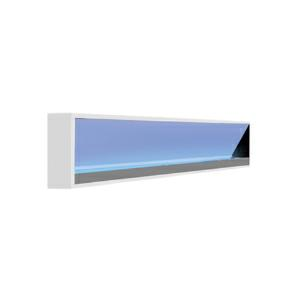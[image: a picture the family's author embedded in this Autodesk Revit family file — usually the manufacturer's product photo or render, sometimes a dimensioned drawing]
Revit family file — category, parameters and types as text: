
# Revit family: 3f_filippi_-_3f_violetta_uv-c_parete_3f_filippi_-_9302_-_3f_violetta_uvc_wall_1x30_t8_s-l_l925
name_source: partatom
category: Lighting Fixtures
units: mm (PartAtom-declared; Revit-internal decimal feet)

## family parameters
Cut with Voids When Loaded = No
Host = Face
Light Source = No
Part Type = Normal
Room Calculation Point = No
Round Connector Dimension = Use Diameter
Shared = No

## types (1)
- 3F Filippi - 3F Violetta UV-C Parete
    Apparent Load = 0 VA
    Approval mark = ENEC
    Default Elevation = 1800 mm
    Description = Room sterilization device, designed for the use of a T8 germicidal lamp.

ILLUMINOTECHNICAL
Luminous efficiency 62%.
Indirect asymmetric distribution for air sanitization.

SOURCE
Fixtures supplied without germicidal lamps (W/L); below are some lamps available from the main distributors of electrical material.
<ul><li>Osram PURITEC T8 - HNS 30W G13</li>
<li>Philips TUV T8 - TUV 30W 1SL/25 G13</li></ul>
Germicidal lamps are special lamps that produce ultraviolet radiation with domain spectral components in the UV-C range; this radiation modifies the DNA or RNA of microorganisms (bacteria, viruses, germ and mould spores) and prevents them from reproducing or being harmful.
Germicidal lamps emit high intensity UV-C radiation that can cause burns, eye irritation (conjunctivitis) and skin damage (erythema).

MECHANICAL
Body made of steel painted white with antimicrobial powder paint.
The particular paint, in addition to the antimicrobial properties, offers protection and decoration typical of a high-performance powder paint and is specific for use in areas where it is necessary to guarantee a high level of cleanliness, for example in the medical, food, public recreational sports areas and for crowded places such as public transport, airports, schools, etc.
The development and spread of microbes such as bacteria, and mould can affect the operation of a product, be responsible for degradation, bad smells and stains.
Cleaning actions are used to eliminate the presence of bacteria on products.
However, between one cleaning cycle and another microbes multiply on surfaces.
The antimicrobial protection acts between cleaning cycles to provide products with further defence against the development of bacteria.
Recuperator in satin anodised aluminium to avoid annoying reflections.
Internal black end caps.
Dimensions: 925x70 mm, height 180 mm. Weight 2.82 kg.
IP20 protection degree.
Glow-wire test resistance 960°C.

ELECTRICAL
EEI A2 Electronic wiring 230V-50/60Hz, class I.
Lamp warm start.
Double insulation silicone cabling with high resistance to UV.
Power of the luminaire 34 W.
CE - IEC 60598-1 - EN 60598-1.
Ambient temperature from 0°C to +25°C.

INSTALLATION
Wall.
Indirect asymmetric distribution for air sanitisation.
Mandatory orientation of the fixture with the lamp at the bottom; installation height of no less than 2 metres from the ground.

APPLICATIONS
Room disinfection fixtures designed to be used with germicidal lamps.

WARNING
The product is designed to be fitted with germicidal lamps with Photobiological risk RG3 (IEC 62471) that emit high intensity UV-C radiation that can cause burns, eye irritation (conjunctivitis) and skin damage (erythema).
<ul><li>Avoid exposure to the skin and eyes to direct or reflected radiation without the use of Personal Protective Equipment (PPE).</li>
<li>Light fixtures that use these type of lamps must be turned on and used only in the absence of people, animals and plants.</li>
<li>Security procedures must be implemented that protect workers of any kind who access rooms where fixtures that emit UV-C radiation are installed; personnel must be suitably shielded from the radiation emitted.</li>
<li>Workers must be informed, be aware of safety procedures and respect them with awareness. It is essential to prevent unprotected people from accessing these rooms in the event the lamps are operational.</li></ul>
A particularly effective safety measure in this regard is to arrange for the lamps to turn on only using special key switches and that these are only entrusted to adequately trained staff.
UV-C rays are similar to sunlight even though they do not transmit heat.
Like sun rays they can nevertheless tend to yellow plastic material exposed for a long time, especially if white in colour and cause alterations to many materials.
Luminaire designed for disposal/recycling at end-of-life.
    Height = 180 mm  [stored 0.590551 ft]
    Lamp = 0 x
    Length = 925 mm
    Luminous efficacy = 0 lm/W
    Manufacturer = 3F Filippi
    ModVariant = No
    Model = 3F Filippi - 9302 - 3F Violetta UVC WALL 1x30 T8 S-L L925
    Mounting Place = Ceiling
    Mounting Type = Surface mounted
    Number of Poles = 1
    OnlyDefault = Yes
    Power Factor = 1
    Product Name = 3F Filippi - 3F Violetta UV-C Parete
    Product group = Accessories
    ProductGroupID = 98
    Protection Class = Protection class I
    Protection Degree = IP 20
    RLX_Detail_Level = 1
    RLX_Emergency_Light_Flux = 0 lm
    RLX_Emergency_Type = 0
    RLX_Emergency_Type_DB = No
    RlxData = <blob elided: 31453 chars, md5=c198f63a>
    Standby Power = 0 W
    System Light Flux = 0 lm
    System Power = 0 W
    Type Comments = Product without accessories
    Type Image = 3ffilippi_3f_violetta_uvc_parete.jpg
    URL = http://relux.com
    VarID = ---
    Voltage = 0 V
    Weight = 0.00 kg
    Width = 70 mm

note: [stored X ft] marks values corroborated as IEEE doubles in the binary element streams (Revit-internal decimal feet)

## geometry (parser evidence)
native form markers: Blend x4, Sweep x10
no freeform markers — native parametric forms only
